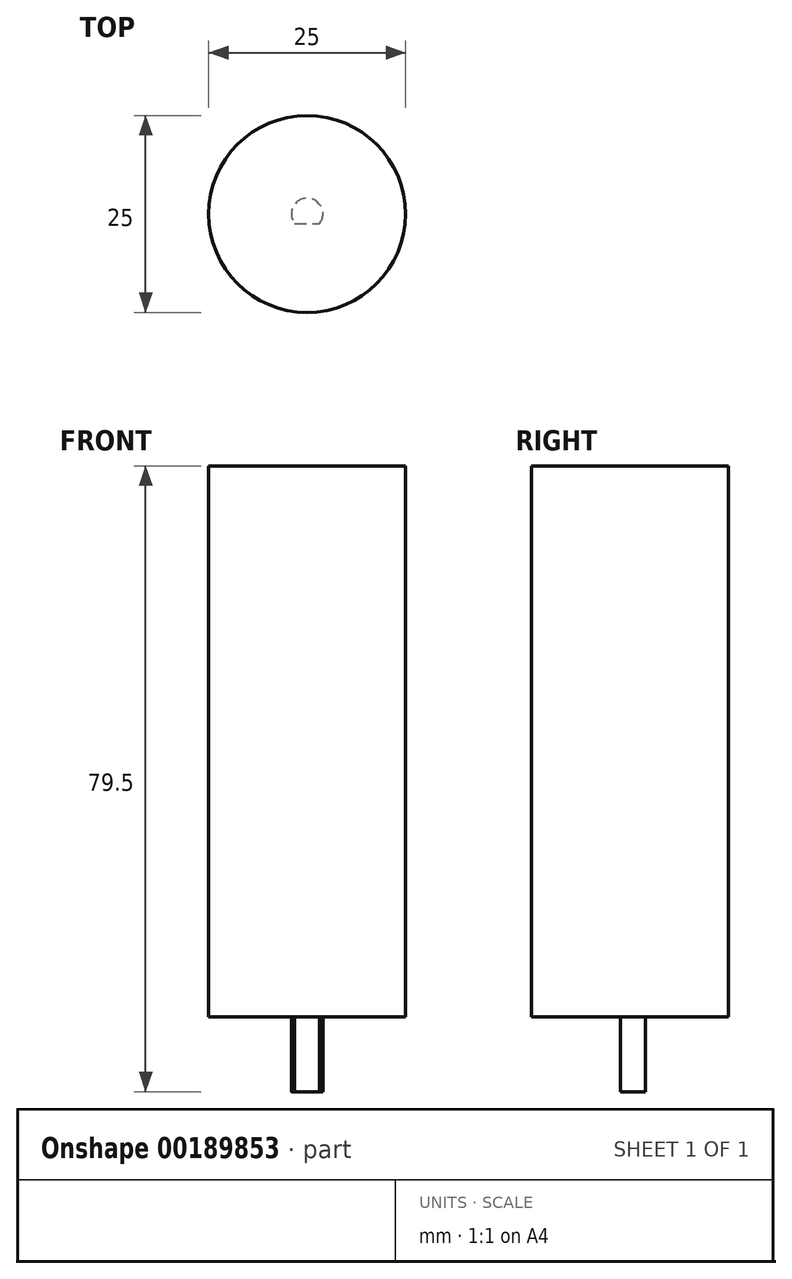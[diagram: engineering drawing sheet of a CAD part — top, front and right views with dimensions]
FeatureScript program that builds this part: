
annotation { "Feature Type Name" : "Feature", "Feature Type Description" : "" }
export const myFeature = defineFeature(function(context is Context, id is Id, definition is map)
    precondition{}
    {
        {
            var Q0;
            Q0=qCreatedBy(makeId("Top.planeOp"),FACE);
            var sketch = newSketch(context, id + "F0", { "sketchPlane" : qUnion([Q0])});
            skCircle(sketch, "E0", {"center": v(0, 0) * mm, "radius": 12.5 * mm});
            skSolve(sketch);
        }
        {
            var Q0;
            Q0=makeQuery(id+"F0.imprint","IMPRINT",FACE,{"disambiguationData":[TD([[makeQuery(id+"F0.imprint","IMPRINT",EDGE,{"derivedFrom":sQuery(id+"F0.wireOp",EDGE,"E0")}),1.0]])]});
            extrude(context, id + "F1", {"entities" : qUnion([Q0]), "depth" : 70 * mm});
        }
        {
            var Q0;
            Q0=makeQuery(id+"F1.opExtrude","CAP_FACE",FACE,{"disambiguationData":[OSD([sQuery(id+"F0.wireOp",EDGE,"E0")])],"isStart":true});
            var sketch = newSketch(context, id + "F2", { "sketchPlane" : qUnion([Q0])});
            skCircle(sketch, "E1", {"center": v(0, 0) * mm, "radius": 2 * mm});
            skLineSegment(sketch, "E2", {"start": v(-1.6, 1.2) * mm, "end": v(1.6, 1.2) * mm});
            skSolve(sketch);
        }
        {
            var Q0;
            {var subQ0=sQuery(id+"F2.wireOp",EDGE,"E2");Q0=makeQuery(id+"F2.imprint","IMPRINT",FACE,{"disambiguationData":[TD([[makeQuery(id+"F2.imprint","IMPRINT",EDGE,{"derivedFrom":subQ0}),-1.0]])]});}
            extrude(context, id + "F3", {"entities" : qUnion([Q0]), "operationType" : NewBodyOperationType.ADD, "depth" : 9.5 * mm});
        }
    });
